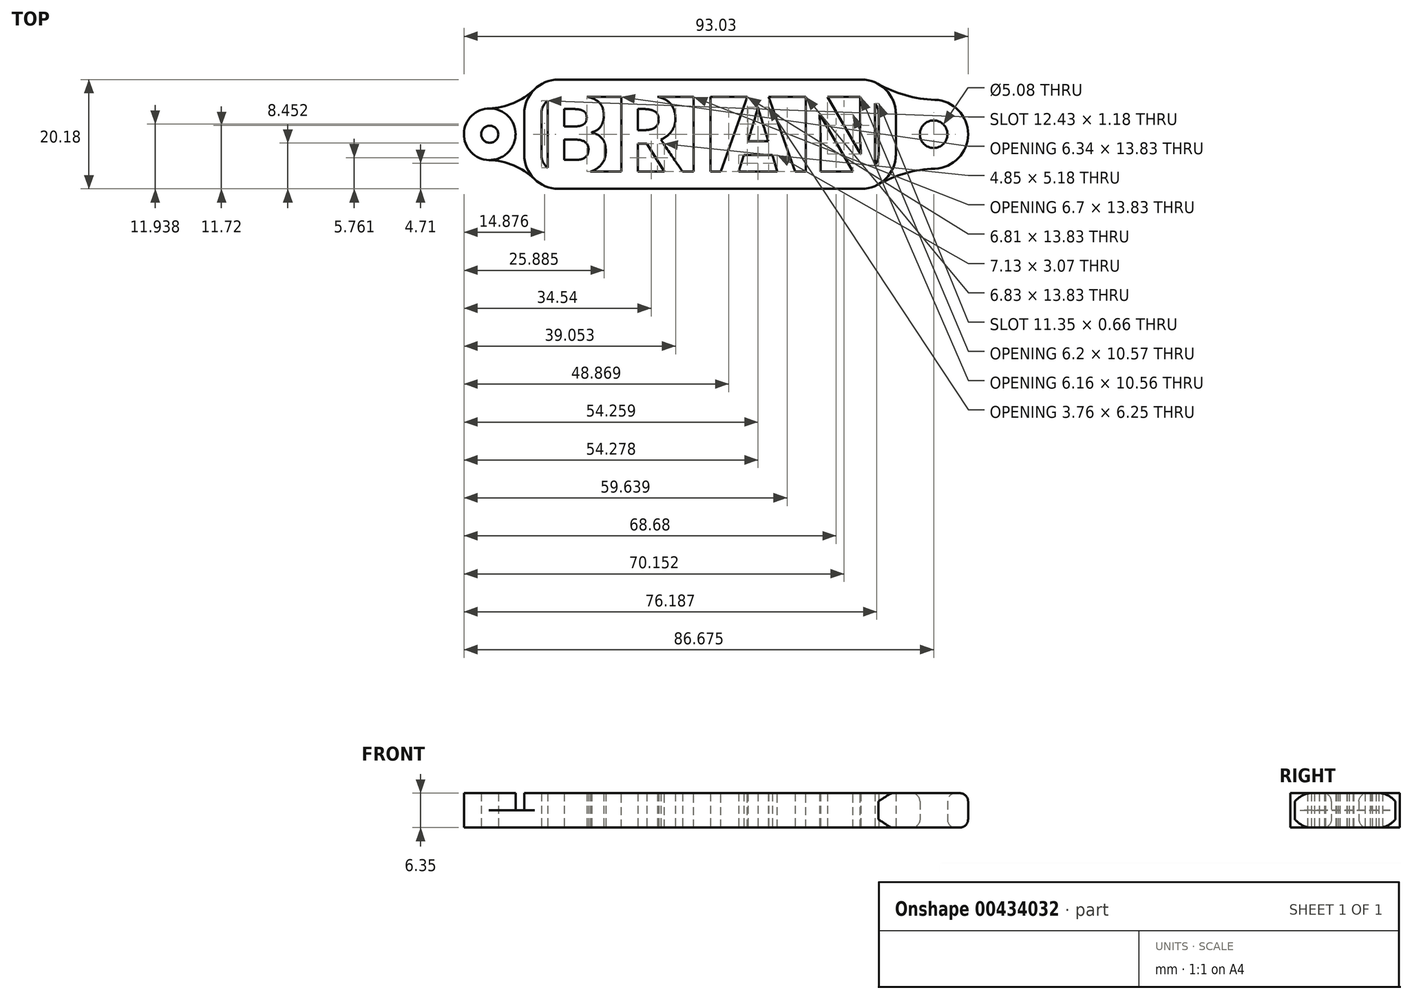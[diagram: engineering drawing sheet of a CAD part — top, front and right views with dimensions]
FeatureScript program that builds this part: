
annotation { "Feature Type Name" : "Feature", "Feature Type Description" : "" }
export const myFeature = defineFeature(function(context is Context, id is Id, definition is map)
    precondition{}
    {
        {
            var Q0;
            Q0=qCreatedBy(makeId("Top.planeOp"),FACE);
            var sketch = newSketch(context, id + "F0", { "sketchPlane" : qUnion([Q0])});
            skText(sketch, "E0", { "text": "BRIAN", "fontName": "OpenSans-Bold.ttf"});
            skLineSegment(sketch, "E1", {"start": v(-31.75, 7.28) * mm, "end": v(31.75, -7.28) * mm, "construction": true});
            const initialGuessF0  = {"E0": [-0.03175, -0.00728, 1, 0, 0.01456]};
            skSetInitialGuess(sketch, initialGuessF0);
            skSolve(sketch);
        }
        {
            var Q0;
            Q0=qCreatedBy(makeId("Top.planeOp"),FACE);
            var sketch = newSketch(context, id + "F1", { "sketchPlane" : qUnion([Q0])});
            skLineSegment(sketch, "E2.bottom", {"start": v(27.94, 10.1) * mm, "end": v(-27.94, 10.1) * mm});
            skLineSegment(sketch, "E2.top", {"start": v(27.94, -10.1) * mm, "end": v(-27.94, -10.1) * mm});
            skLineSegment(sketch, "E2.left", {"start": v(34.3, 3.74) * mm, "end": v(34.3, -3.74) * mm});
            skLineSegment(sketch, "E2.right", {"start": v(-34.3, 3.74) * mm, "end": v(-34.3, -3.74) * mm});
            skPoint(sketch, "E2.middle", {"position": v(0, 0) * mm});
            skPoint(sketch, "E3.visualSharp", {"position": v(-34.3, 10.1) * mm});
            skArc(sketch, "E3.filletArc", {"start": v(-27.94, 10.1) * mm, "mid": v(-32.43, 8.23) * mm, "end": v(-34.3, 3.74) * mm});
            skPoint(sketch, "E4.visualSharp", {"position": v(-34.3, -10.1) * mm});
            skArc(sketch, "E4.filletArc", {"start": v(-34.3, -3.74) * mm, "mid": v(-32.43, -8.23) * mm, "end": v(-27.94, -10.1) * mm});
            skPoint(sketch, "E5.visualSharp", {"position": v(34.3, -10.1) * mm});
            skArc(sketch, "E5.filletArc", {"start": v(27.94, -10.1) * mm, "mid": v(32.43, -8.23) * mm, "end": v(34.3, -3.74) * mm});
            skPoint(sketch, "E6.visualSharp", {"position": v(34.3, 10.1) * mm});
            skArc(sketch, "E6.filletArc", {"start": v(34.3, 3.74) * mm, "mid": v(32.43, 8.23) * mm, "end": v(27.94, 10.1) * mm});
            skArc(sketch, "E7.0", {"start": v(31.12, 3.74) * mm, "mid": v(30.19, 5.99) * mm, "end": v(27.94, 6.92) * mm});
            skLineSegment(sketch, "E7.1", {"start": v(31.12, 3.74) * mm, "end": v(31.12, -3.74) * mm});
            skLineSegment(sketch, "E7.2", {"start": v(27.94, 6.92) * mm, "end": v(-27.94, 6.92) * mm});
            skArc(sketch, "E7.3", {"start": v(27.94, -6.92) * mm, "mid": v(30.19, -5.99) * mm, "end": v(31.12, -3.74) * mm});
            skArc(sketch, "E7.4", {"start": v(-27.94, 6.92) * mm, "mid": v(-30.19, 5.99) * mm, "end": v(-31.12, 3.74) * mm});
            skLineSegment(sketch, "E7.5", {"start": v(-31.12, 3.74) * mm, "end": v(-31.12, -3.74) * mm});
            skArc(sketch, "E7.6", {"start": v(-31.12, -3.74) * mm, "mid": v(-30.19, -5.99) * mm, "end": v(-27.94, -6.92) * mm});
            skLineSegment(sketch, "E7.7", {"start": v(27.94, -6.92) * mm, "end": v(-27.94, -6.92) * mm});
            skSolve(sketch);
        }
        {
            var Q0;
            Q0=makeQuery(id+"F0.imprint","IMPRINT",FACE,{"disambiguationData":[TD([[makeQuery(id+"F0.imprint","IMPRINT",EDGE,{"derivedFrom":sQuery(id+"F0.wireOp",EDGE,"E0.sketch_text.stroke-0")}),-1.0]])]});
            var Q1;
            Q1=makeQuery(id+"F0.imprint","IMPRINT",FACE,{"disambiguationData":[TD([[makeQuery(id+"F0.imprint","IMPRINT",EDGE,{"derivedFrom":sQuery(id+"F0.wireOp",EDGE,"E0.sketch_text.stroke-25")}),-1.0]])]});
            var Q2;
            Q2=makeQuery(id+"F0.imprint","IMPRINT",FACE,{"disambiguationData":[TD([[makeQuery(id+"F0.imprint","IMPRINT",EDGE,{"derivedFrom":sQuery(id+"F0.wireOp",EDGE,"E0.sketch_text.stroke-44")}),-1.0]])]});
            var Q3;
            Q3=makeQuery(id+"F0.imprint","IMPRINT",FACE,{"disambiguationData":[TD([[makeQuery(id+"F0.imprint","IMPRINT",EDGE,{"derivedFrom":sQuery(id+"F0.wireOp",EDGE,"E0.sketch_text.stroke-48")}),-1.0]])]});
            var Q4;
            Q4=makeQuery(id+"F0.imprint","IMPRINT",FACE,{"disambiguationData":[TD([[makeQuery(id+"F0.imprint","IMPRINT",EDGE,{"derivedFrom":sQuery(id+"F0.wireOp",EDGE,"E0.sketch_text.stroke-60")}),-1.0]])]});
            var Q5;
            Q5=makeQuery(id+"F1.imprint","IMPRINT",FACE,{"disambiguationData":[TD([[makeQuery(id+"F1.imprint","IMPRINT",EDGE,{"derivedFrom":sQuery(id+"F1.wireOp",EDGE,"E2.bottom")}),1.0]])]});
            extrude(context, id + "F2", {"entities" : qUnion([Q0, Q1, Q2, Q3, Q4, Q5]), "depth" : 6.35 * mm});
        }
        {
            var Q0;
            Q0=makeQuery(id+"F2.opExtrude","SWEPT_BODY",BODY,{"disambiguationData":[OSD([sQuery(id+"F0.wireOp",EDGE,"E0.sketch_text.stroke-0"),sQuery(id+"F0.wireOp",EDGE,"E0.sketch_text.stroke-1"),sQuery(id+"F0.wireOp",EDGE,"E0.sketch_text.stroke-2"),sQuery(id+"F0.wireOp",EDGE,"E0.sketch_text.stroke-3"),sQuery(id+"F0.wireOp",EDGE,"E0.sketch_text.stroke-4"),sQuery(id+"F0.wireOp",EDGE,"E0.sketch_text.stroke-5"),sQuery(id+"F0.wireOp",EDGE,"E0.sketch_text.stroke-6"),sQuery(id+"F0.wireOp",EDGE,"E0.sketch_text.stroke-7"),sQuery(id+"F0.wireOp",EDGE,"E0.sketch_text.stroke-8"),sQuery(id+"F0.wireOp",EDGE,"E0.sketch_text.stroke-9"),sQuery(id+"F0.wireOp",EDGE,"E0.sketch_text.stroke-10"),sQuery(id+"F0.wireOp",EDGE,"E0.sketch_text.stroke-11"),sQuery(id+"F0.wireOp",EDGE,"E0.sketch_text.stroke-12"),sQuery(id+"F0.wireOp",EDGE,"E0.sketch_text.stroke-13"),sQuery(id+"F0.wireOp",EDGE,"E0.sketch_text.stroke-14"),sQuery(id+"F0.wireOp",EDGE,"E0.sketch_text.stroke-15"),sQuery(id+"F0.wireOp",EDGE,"E0.sketch_text.stroke-16"),sQuery(id+"F0.wireOp",EDGE,"E0.sketch_text.stroke-17"),sQuery(id+"F0.wireOp",EDGE,"E0.sketch_text.stroke-18"),sQuery(id+"F0.wireOp",EDGE,"E0.sketch_text.stroke-19"),sQuery(id+"F0.wireOp",EDGE,"E0.sketch_text.stroke-20"),sQuery(id+"F0.wireOp",EDGE,"E0.sketch_text.stroke-21"),sQuery(id+"F0.wireOp",EDGE,"E0.sketch_text.stroke-22"),sQuery(id+"F0.wireOp",EDGE,"E0.sketch_text.stroke-23"),sQuery(id+"F0.wireOp",EDGE,"E0.sketch_text.stroke-24")])]});
            var Q1;
            Q1=makeQuery(id+"F2.opExtrude","SWEPT_BODY",BODY,{"disambiguationData":[OSD([sQuery(id+"F0.wireOp",EDGE,"E0.sketch_text.stroke-25"),sQuery(id+"F0.wireOp",EDGE,"E0.sketch_text.stroke-26"),sQuery(id+"F0.wireOp",EDGE,"E0.sketch_text.stroke-27"),sQuery(id+"F0.wireOp",EDGE,"E0.sketch_text.stroke-28"),sQuery(id+"F0.wireOp",EDGE,"E0.sketch_text.stroke-29"),sQuery(id+"F0.wireOp",EDGE,"E0.sketch_text.stroke-30"),sQuery(id+"F0.wireOp",EDGE,"E0.sketch_text.stroke-31"),sQuery(id+"F0.wireOp",EDGE,"E0.sketch_text.stroke-32"),sQuery(id+"F0.wireOp",EDGE,"E0.sketch_text.stroke-33"),sQuery(id+"F0.wireOp",EDGE,"E0.sketch_text.stroke-34"),sQuery(id+"F0.wireOp",EDGE,"E0.sketch_text.stroke-35"),sQuery(id+"F0.wireOp",EDGE,"E0.sketch_text.stroke-36"),sQuery(id+"F0.wireOp",EDGE,"E0.sketch_text.stroke-37"),sQuery(id+"F0.wireOp",EDGE,"E0.sketch_text.stroke-38"),sQuery(id+"F0.wireOp",EDGE,"E0.sketch_text.stroke-39"),sQuery(id+"F0.wireOp",EDGE,"E0.sketch_text.stroke-40"),sQuery(id+"F0.wireOp",EDGE,"E0.sketch_text.stroke-41"),sQuery(id+"F0.wireOp",EDGE,"E0.sketch_text.stroke-42"),sQuery(id+"F0.wireOp",EDGE,"E0.sketch_text.stroke-43")])]});
            var Q2;
            Q2=makeQuery(id+"F2.opExtrude","SWEPT_BODY",BODY,{"disambiguationData":[OSD([sQuery(id+"F0.wireOp",EDGE,"E0.sketch_text.stroke-44"),sQuery(id+"F0.wireOp",EDGE,"E0.sketch_text.stroke-45"),sQuery(id+"F0.wireOp",EDGE,"E0.sketch_text.stroke-46"),sQuery(id+"F0.wireOp",EDGE,"E0.sketch_text.stroke-47")])]});
            var Q3;
            Q3=makeQuery(id+"F2.opExtrude","SWEPT_BODY",BODY,{"disambiguationData":[OSD([sQuery(id+"F0.wireOp",EDGE,"E0.sketch_text.stroke-48"),sQuery(id+"F0.wireOp",EDGE,"E0.sketch_text.stroke-49"),sQuery(id+"F0.wireOp",EDGE,"E0.sketch_text.stroke-50"),sQuery(id+"F0.wireOp",EDGE,"E0.sketch_text.stroke-51"),sQuery(id+"F0.wireOp",EDGE,"E0.sketch_text.stroke-52"),sQuery(id+"F0.wireOp",EDGE,"E0.sketch_text.stroke-53"),sQuery(id+"F0.wireOp",EDGE,"E0.sketch_text.stroke-54"),sQuery(id+"F0.wireOp",EDGE,"E0.sketch_text.stroke-55"),sQuery(id+"F0.wireOp",EDGE,"E0.sketch_text.stroke-56"),sQuery(id+"F0.wireOp",EDGE,"E0.sketch_text.stroke-57"),sQuery(id+"F0.wireOp",EDGE,"E0.sketch_text.stroke-58"),sQuery(id+"F0.wireOp",EDGE,"E0.sketch_text.stroke-59")])]});
            var Q4;
            Q4=makeQuery(id+"F2.opExtrude","SWEPT_BODY",BODY,{"disambiguationData":[OSD([sQuery(id+"F0.wireOp",EDGE,"E0.sketch_text.stroke-60"),sQuery(id+"F0.wireOp",EDGE,"E0.sketch_text.stroke-61"),sQuery(id+"F0.wireOp",EDGE,"E0.sketch_text.stroke-62"),sQuery(id+"F0.wireOp",EDGE,"E0.sketch_text.stroke-63"),sQuery(id+"F0.wireOp",EDGE,"E0.sketch_text.stroke-64"),sQuery(id+"F0.wireOp",EDGE,"E0.sketch_text.stroke-65"),sQuery(id+"F0.wireOp",EDGE,"E0.sketch_text.stroke-66"),sQuery(id+"F0.wireOp",EDGE,"E0.sketch_text.stroke-67"),sQuery(id+"F0.wireOp",EDGE,"E0.sketch_text.stroke-68"),sQuery(id+"F0.wireOp",EDGE,"E0.sketch_text.stroke-69"),sQuery(id+"F0.wireOp",EDGE,"E0.sketch_text.stroke-70"),sQuery(id+"F0.wireOp",EDGE,"E0.sketch_text.stroke-71"),sQuery(id+"F0.wireOp",EDGE,"E0.sketch_text.stroke-72"),sQuery(id+"F0.wireOp",EDGE,"E0.sketch_text.stroke-73")])]});
            var Q5;
            Q5=makeQuery(id+"F2.opExtrude","SWEPT_BODY",BODY,{"disambiguationData":[OSD([sQuery(id+"F1.wireOp",EDGE,"E2.bottom"),sQuery(id+"F1.wireOp",EDGE,"E2.top"),sQuery(id+"F1.wireOp",EDGE,"E2.left"),sQuery(id+"F1.wireOp",EDGE,"E2.right"),sQuery(id+"F1.wireOp",EDGE,"E3.filletArc"),sQuery(id+"F1.wireOp",EDGE,"E4.filletArc"),sQuery(id+"F1.wireOp",EDGE,"E5.filletArc"),sQuery(id+"F1.wireOp",EDGE,"E6.filletArc"),sQuery(id+"F1.wireOp",EDGE,"E7.0"),sQuery(id+"F1.wireOp",EDGE,"E7.1"),sQuery(id+"F1.wireOp",EDGE,"E7.2"),sQuery(id+"F1.wireOp",EDGE,"E7.3"),sQuery(id+"F1.wireOp",EDGE,"E7.4"),sQuery(id+"F1.wireOp",EDGE,"E7.5"),sQuery(id+"F1.wireOp",EDGE,"E7.6"),sQuery(id+"F1.wireOp",EDGE,"E7.7")])]});
            booleanBodies(context, id + "F3", {"operationType" : BooleanOperationType.UNION, "tools" : qUnion([Q0, Q1, Q2, Q3, Q4, Q5])});
        }
        {
            var Q0;
            Q0=qCreatedBy(makeId("Top.planeOp"),FACE);
            var sketch = newSketch(context, id + "F4", { "sketchPlane" : qUnion([Q0])});
            skCircle(sketch, "E8", {"center": v(-40.64, 0) * mm, "radius": 1.59 * mm});
            skCircle(sketch, "E9", {"center": v(-40.64, 0) * mm, "radius": 4.76 * mm});
            skArc(sketch, "E10", {"start": v(-40.78, 4.76) * mm, "mid": v(-36.23, 5.75) * mm, "end": v(-32.35, 8.31) * mm});
            skArc(sketch, "E11", {"start": v(-32.35, -8.31) * mm, "mid": v(-36.23, -5.75) * mm, "end": v(-40.78, -4.76) * mm});
            skLineSegment(sketch, "E12.0", {"start": v(-34.3, 3.74) * mm, "end": v(-34.3, -3.74) * mm});
            skArc(sketch, "E12.1", {"start": v(-32.35, 8.31) * mm, "mid": v(-33.78, 6.23) * mm, "end": v(-34.3, 3.74) * mm});
            skArc(sketch, "E12.2", {"start": v(-34.3, -3.74) * mm, "mid": v(-33.78, -6.23) * mm, "end": v(-32.35, -8.31) * mm});
            skPoint(sketch, "E13.orphan", {"position": v(-27.94, 10.1) * mm});
            skPoint(sketch, "E14.orphan", {"position": v(-27.94, -10.1) * mm});
            skSolve(sketch);
        }
        {
            var Q0;
            {var subQ1=sQuery(id+"F4.wireOp",EDGE,"E10");Q0=makeQuery(id+"F4.imprint","IMPRINT",FACE,{"disambiguationData":[TD([[makeQuery(id+"F4.imprint","IMPRINT",EDGE,{"derivedFrom":subQ1}),-1.0]])]});}
            extrude(context, id + "F5", {"entities" : qUnion([Q0]), "operationType" : NewBodyOperationType.ADD, "depth" : 3.17 * mm});
        }
        {
            var Q0;
            Q0=makeQuery(id+"F4.imprint","IMPRINT",FACE,{"disambiguationData":[TD([[makeQuery(id+"F4.imprint","IMPRINT",EDGE,{"derivedFrom":sQuery(id+"F4.wireOp",EDGE,"E8")}),-1.0]])]});
            extrude(context, id + "F6", {"entities" : qUnion([Q0]), "operationType" : NewBodyOperationType.ADD, "depth" : 6.35 * mm});
        }
        {
            var Q0;
            Q0=qCreatedBy(makeId("Top.planeOp"),FACE);
            var sketch = newSketch(context, id + "F7", { "sketchPlane" : qUnion([Q0])});
            skCircle(sketch, "E15", {"center": v(41.28, 0) * mm, "radius": 6.35 * mm});
            skCircle(sketch, "E16", {"center": v(41.28, 0) * mm, "radius": 2.54 * mm});
            skArc(sketch, "E17", {"start": v(31.06, 9.27) * mm, "mid": v(36.1, 7.18) * mm, "end": v(41.5, 6.35) * mm});
            skArc(sketch, "E18", {"start": v(41.5, -6.35) * mm, "mid": v(36.1, -7.18) * mm, "end": v(31.06, -9.27) * mm});
            skArc(sketch, "E19.0", {"start": v(31.06, -9.27) * mm, "mid": v(33.42, -6.95) * mm, "end": v(34.3, -3.74) * mm});
            skLineSegment(sketch, "E20.0", {"start": v(34.3, 3.74) * mm, "end": v(34.3, -3.74) * mm});
            skArc(sketch, "E21.0", {"start": v(34.3, 3.74) * mm, "mid": v(33.42, 6.95) * mm, "end": v(31.06, 9.27) * mm});
            skPoint(sketch, "E22.orphan", {"position": v(27.94, -10.1) * mm});
            skPoint(sketch, "E23.orphan", {"position": v(27.94, 10.1) * mm});
            skSolve(sketch);
        }
        {
            var Q0;
            Q0=makeQuery(id+"F7.imprint","IMPRINT",FACE,{"disambiguationData":[TD([[makeQuery(id+"F7.imprint","IMPRINT",EDGE,{"derivedFrom":sQuery(id+"F7.wireOp",EDGE,"E15")}),1.0]])]});
            var Q1;
            {var subQ1=sQuery(id+"F7.wireOp",EDGE,"E17");Q1=makeQuery(id+"F7.imprint","IMPRINT",FACE,{"disambiguationData":[TD([[makeQuery(id+"F7.imprint","IMPRINT",EDGE,{"derivedFrom":subQ1}),-1.0]])]});}
            var Q2;
            Q2=makeQuery(id+"F3.opBoolean","MERGE",FACE,{"derivedFrom":[makeQuery(id+"F2.opExtrude","CAP_FACE",FACE,{"disambiguationData":[OSD([sQuery(id+"F0.wireOp",EDGE,"E0.sketch_text.stroke-0"),sQuery(id+"F0.wireOp",EDGE,"E0.sketch_text.stroke-1"),sQuery(id+"F0.wireOp",EDGE,"E0.sketch_text.stroke-2"),sQuery(id+"F0.wireOp",EDGE,"E0.sketch_text.stroke-3"),sQuery(id+"F0.wireOp",EDGE,"E0.sketch_text.stroke-4"),sQuery(id+"F0.wireOp",EDGE,"E0.sketch_text.stroke-5"),sQuery(id+"F0.wireOp",EDGE,"E0.sketch_text.stroke-6"),sQuery(id+"F0.wireOp",EDGE,"E0.sketch_text.stroke-7"),sQuery(id+"F0.wireOp",EDGE,"E0.sketch_text.stroke-8"),sQuery(id+"F0.wireOp",EDGE,"E0.sketch_text.stroke-9"),sQuery(id+"F0.wireOp",EDGE,"E0.sketch_text.stroke-10"),sQuery(id+"F0.wireOp",EDGE,"E0.sketch_text.stroke-11"),sQuery(id+"F0.wireOp",EDGE,"E0.sketch_text.stroke-12"),sQuery(id+"F0.wireOp",EDGE,"E0.sketch_text.stroke-13"),sQuery(id+"F0.wireOp",EDGE,"E0.sketch_text.stroke-14"),sQuery(id+"F0.wireOp",EDGE,"E0.sketch_text.stroke-15"),sQuery(id+"F0.wireOp",EDGE,"E0.sketch_text.stroke-16"),sQuery(id+"F0.wireOp",EDGE,"E0.sketch_text.stroke-17"),sQuery(id+"F0.wireOp",EDGE,"E0.sketch_text.stroke-18"),sQuery(id+"F0.wireOp",EDGE,"E0.sketch_text.stroke-19"),sQuery(id+"F0.wireOp",EDGE,"E0.sketch_text.stroke-20"),sQuery(id+"F0.wireOp",EDGE,"E0.sketch_text.stroke-21"),sQuery(id+"F0.wireOp",EDGE,"E0.sketch_text.stroke-22"),sQuery(id+"F0.wireOp",EDGE,"E0.sketch_text.stroke-23"),sQuery(id+"F0.wireOp",EDGE,"E0.sketch_text.stroke-24")])],"isStart":false}),makeQuery(id+"F2.opExtrude","CAP_FACE",FACE,{"disambiguationData":[OSD([sQuery(id+"F0.wireOp",EDGE,"E0.sketch_text.stroke-25"),sQuery(id+"F0.wireOp",EDGE,"E0.sketch_text.stroke-26"),sQuery(id+"F0.wireOp",EDGE,"E0.sketch_text.stroke-27"),sQuery(id+"F0.wireOp",EDGE,"E0.sketch_text.stroke-28"),sQuery(id+"F0.wireOp",EDGE,"E0.sketch_text.stroke-29"),sQuery(id+"F0.wireOp",EDGE,"E0.sketch_text.stroke-30"),sQuery(id+"F0.wireOp",EDGE,"E0.sketch_text.stroke-31"),sQuery(id+"F0.wireOp",EDGE,"E0.sketch_text.stroke-32"),sQuery(id+"F0.wireOp",EDGE,"E0.sketch_text.stroke-33"),sQuery(id+"F0.wireOp",EDGE,"E0.sketch_text.stroke-34"),sQuery(id+"F0.wireOp",EDGE,"E0.sketch_text.stroke-35"),sQuery(id+"F0.wireOp",EDGE,"E0.sketch_text.stroke-36"),sQuery(id+"F0.wireOp",EDGE,"E0.sketch_text.stroke-37"),sQuery(id+"F0.wireOp",EDGE,"E0.sketch_text.stroke-38"),sQuery(id+"F0.wireOp",EDGE,"E0.sketch_text.stroke-39"),sQuery(id+"F0.wireOp",EDGE,"E0.sketch_text.stroke-40"),sQuery(id+"F0.wireOp",EDGE,"E0.sketch_text.stroke-41"),sQuery(id+"F0.wireOp",EDGE,"E0.sketch_text.stroke-42"),sQuery(id+"F0.wireOp",EDGE,"E0.sketch_text.stroke-43")])],"isStart":false}),makeQuery(id+"F2.opExtrude","CAP_FACE",FACE,{"disambiguationData":[OSD([sQuery(id+"F0.wireOp",EDGE,"E0.sketch_text.stroke-44"),sQuery(id+"F0.wireOp",EDGE,"E0.sketch_text.stroke-45"),sQuery(id+"F0.wireOp",EDGE,"E0.sketch_text.stroke-46"),sQuery(id+"F0.wireOp",EDGE,"E0.sketch_text.stroke-47")])],"isStart":false}),makeQuery(id+"F2.opExtrude","CAP_FACE",FACE,{"disambiguationData":[OSD([sQuery(id+"F0.wireOp",EDGE,"E0.sketch_text.stroke-48"),sQuery(id+"F0.wireOp",EDGE,"E0.sketch_text.stroke-49"),sQuery(id+"F0.wireOp",EDGE,"E0.sketch_text.stroke-50"),sQuery(id+"F0.wireOp",EDGE,"E0.sketch_text.stroke-51"),sQuery(id+"F0.wireOp",EDGE,"E0.sketch_text.stroke-52"),sQuery(id+"F0.wireOp",EDGE,"E0.sketch_text.stroke-53"),sQuery(id+"F0.wireOp",EDGE,"E0.sketch_text.stroke-54"),sQuery(id+"F0.wireOp",EDGE,"E0.sketch_text.stroke-55"),sQuery(id+"F0.wireOp",EDGE,"E0.sketch_text.stroke-56"),sQuery(id+"F0.wireOp",EDGE,"E0.sketch_text.stroke-57"),sQuery(id+"F0.wireOp",EDGE,"E0.sketch_text.stroke-58"),sQuery(id+"F0.wireOp",EDGE,"E0.sketch_text.stroke-59")])],"isStart":false}),makeQuery(id+"F2.opExtrude","CAP_FACE",FACE,{"disambiguationData":[OSD([sQuery(id+"F0.wireOp",EDGE,"E0.sketch_text.stroke-60"),sQuery(id+"F0.wireOp",EDGE,"E0.sketch_text.stroke-61"),sQuery(id+"F0.wireOp",EDGE,"E0.sketch_text.stroke-62"),sQuery(id+"F0.wireOp",EDGE,"E0.sketch_text.stroke-63"),sQuery(id+"F0.wireOp",EDGE,"E0.sketch_text.stroke-64"),sQuery(id+"F0.wireOp",EDGE,"E0.sketch_text.stroke-65"),sQuery(id+"F0.wireOp",EDGE,"E0.sketch_text.stroke-66"),sQuery(id+"F0.wireOp",EDGE,"E0.sketch_text.stroke-67"),sQuery(id+"F0.wireOp",EDGE,"E0.sketch_text.stroke-68"),sQuery(id+"F0.wireOp",EDGE,"E0.sketch_text.stroke-69"),sQuery(id+"F0.wireOp",EDGE,"E0.sketch_text.stroke-70"),sQuery(id+"F0.wireOp",EDGE,"E0.sketch_text.stroke-71"),sQuery(id+"F0.wireOp",EDGE,"E0.sketch_text.stroke-72"),sQuery(id+"F0.wireOp",EDGE,"E0.sketch_text.stroke-73")])],"isStart":false}),makeQuery(id+"F2.opExtrude","CAP_FACE",FACE,{"disambiguationData":[OSD([sQuery(id+"F1.wireOp",EDGE,"E2.bottom"),sQuery(id+"F1.wireOp",EDGE,"E2.top"),sQuery(id+"F1.wireOp",EDGE,"E2.left"),sQuery(id+"F1.wireOp",EDGE,"E2.right"),sQuery(id+"F1.wireOp",EDGE,"E3.filletArc"),sQuery(id+"F1.wireOp",EDGE,"E4.filletArc"),sQuery(id+"F1.wireOp",EDGE,"E5.filletArc"),sQuery(id+"F1.wireOp",EDGE,"E6.filletArc"),sQuery(id+"F1.wireOp",EDGE,"E7.0"),sQuery(id+"F1.wireOp",EDGE,"E7.1"),sQuery(id+"F1.wireOp",EDGE,"E7.2"),sQuery(id+"F1.wireOp",EDGE,"E7.3"),sQuery(id+"F1.wireOp",EDGE,"E7.4"),sQuery(id+"F1.wireOp",EDGE,"E7.5"),sQuery(id+"F1.wireOp",EDGE,"E7.6"),sQuery(id+"F1.wireOp",EDGE,"E7.7")])],"isStart":false})]});
            extrude(context, id + "F8", {"entities" : qUnion([Q0, Q1]), "endBound" : BoundingType.UP_TO_SURFACE, "endBoundEntityFace" : qUnion([Q2]), "depth" : 25.4 * mm});
        }
        {
            var Q0;
            Q0=makeQuery(id+"F8.opExtrude","CAP_EDGE",EDGE,{"disambiguationData":[OSD([sQuery(id+"F7.wireOp",EDGE,"E16")])],"isStart":false});
            var Q1;
            Q1=makeQuery(id+"F8.opExtrude","CAP_EDGE",EDGE,{"disambiguationData":[OSD([sQuery(id+"F7.wireOp",EDGE,"E15")])],"isStart":true});
            var Q2;
            Q2=makeQuery(id+"F8.opExtrude","CAP_EDGE",EDGE,{"disambiguationData":[OSD([sQuery(id+"F7.wireOp",EDGE,"E15")])],"isStart":false});
            var Q3;
            Q3=makeQuery(id+"F8.opExtrude","CAP_EDGE",EDGE,{"disambiguationData":[OSD([sQuery(id+"F7.wireOp",EDGE,"E16")])],"isStart":true});
            fillet(context, id + "F9", {"entities" : qUnion([Q0, Q1, Q2, Q3]), "radius" : 1.52 * mm, "tangentPropagation" : true, "allowEdgeOverflow" : false});
        }
    });
